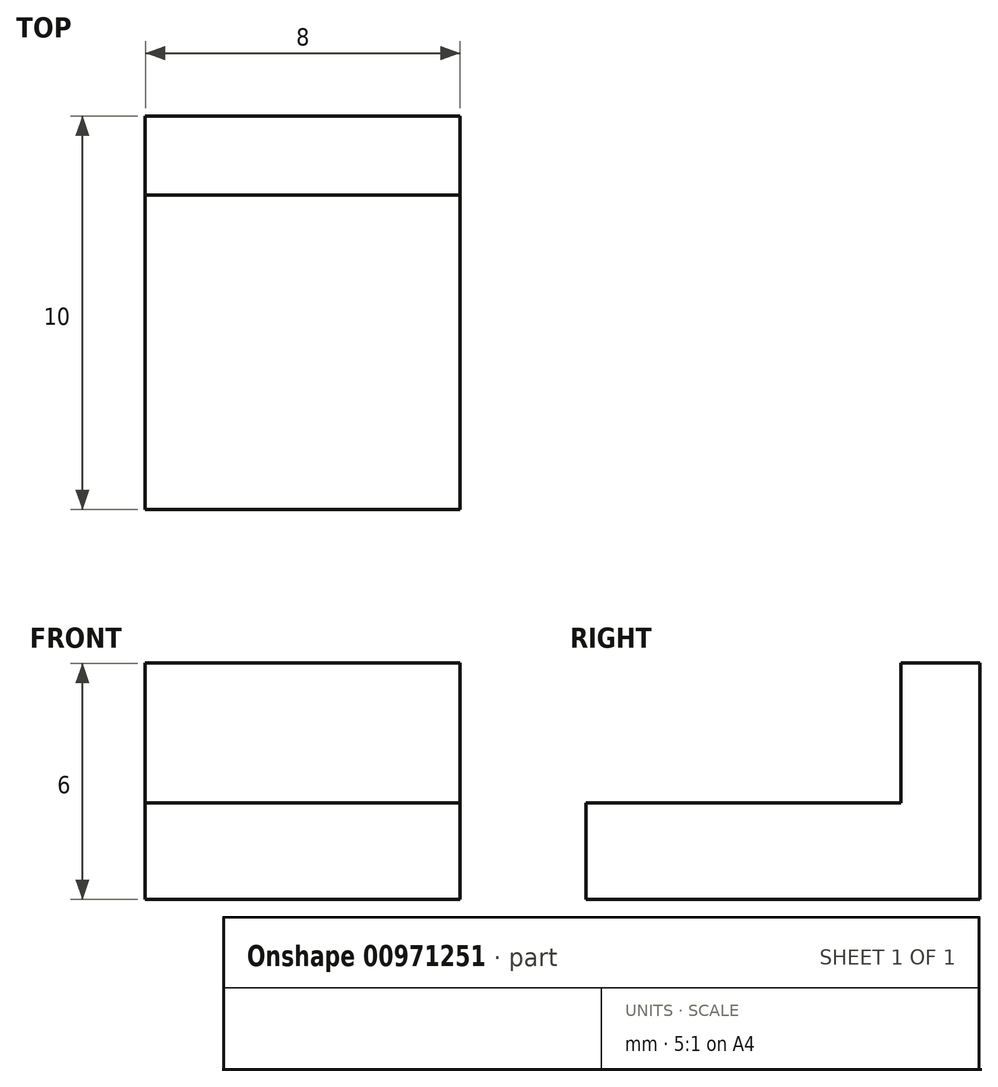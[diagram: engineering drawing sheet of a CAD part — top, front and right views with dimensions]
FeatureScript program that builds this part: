
annotation { "Feature Type Name" : "Feature", "Feature Type Description" : "" }
export const myFeature = defineFeature(function(context is Context, id is Id, definition is map)
    precondition{}
    {
        {
            var Q0;
            Q0=qCreatedBy(makeId("Front.planeOp"),FACE);
            var sketch = newSketch(context, id + "F0", { "sketchPlane" : qUnion([Q0])});
            skLineSegment(sketch, "E0.left", {"start": v(0, 5.88) * mm, "end": v(0, 5.92) * mm});
            skLineSegment(sketch, "E0.right", {"start": v(-2.61, 5.88) * mm, "end": v(-2.61, 5.92) * mm});
            skLineSegment(sketch, "E1.bottom", {"start": v(-4.26, 2.84) * mm, "end": v(3.74, 2.84) * mm});
            skLineSegment(sketch, "E1.top", {"start": v(-4.26, 0.4) * mm, "end": v(3.74, 0.4) * mm});
            skLineSegment(sketch, "E1.left", {"start": v(-4.26, 2.84) * mm, "end": v(-4.26, 0.4) * mm});
            skLineSegment(sketch, "E1.right", {"start": v(3.74, 2.84) * mm, "end": v(3.74, 0.4) * mm});
            skSolve(sketch);
        }
        {
            var Q0;
            Q0 = qSketchRegion(id + "F0", true);
            extrude(context, id + "F1", {"entities" : qUnion([Q0]), "depth" : 8 * mm, "offsetDistance" : 25.4 * mm});
        }
        {
            var Q0;
            Q0=makeQuery(id+"F1.opExtrude","CAP_FACE",FACE,{"disambiguationData":[OSD([sQuery(id+"F0.wireOp",EDGE,"E1.bottom"),sQuery(id+"F0.wireOp",EDGE,"E1.top"),sQuery(id+"F0.wireOp",EDGE,"E1.left"),sQuery(id+"F0.wireOp",EDGE,"E1.right")])],"isStart":true});
            var sketch = newSketch(context, id + "F2", { "sketchPlane" : qUnion([Q0])});
            skLineSegment(sketch, "E2.bottom", {"start": v(-3.74, 0.4) * mm, "end": v(4.26, 0.4) * mm});
            skLineSegment(sketch, "E2.top", {"start": v(-3.74, 6.4) * mm, "end": v(4.26, 6.4) * mm});
            skLineSegment(sketch, "E2.left", {"start": v(-3.74, 0.4) * mm, "end": v(-3.74, 6.4) * mm});
            skLineSegment(sketch, "E2.right", {"start": v(4.26, 0.4) * mm, "end": v(4.26, 6.4) * mm});
            skSolve(sketch);
        }
        {
            var Q0;
            Q0 = qSketchRegion(id + "F2", true);
            extrude(context, id + "F3", {"entities" : qUnion([Q0]), "operationType" : NewBodyOperationType.ADD, "depth" : 2 * mm, "offsetDistance" : 25.4 * mm});
        }
    });
